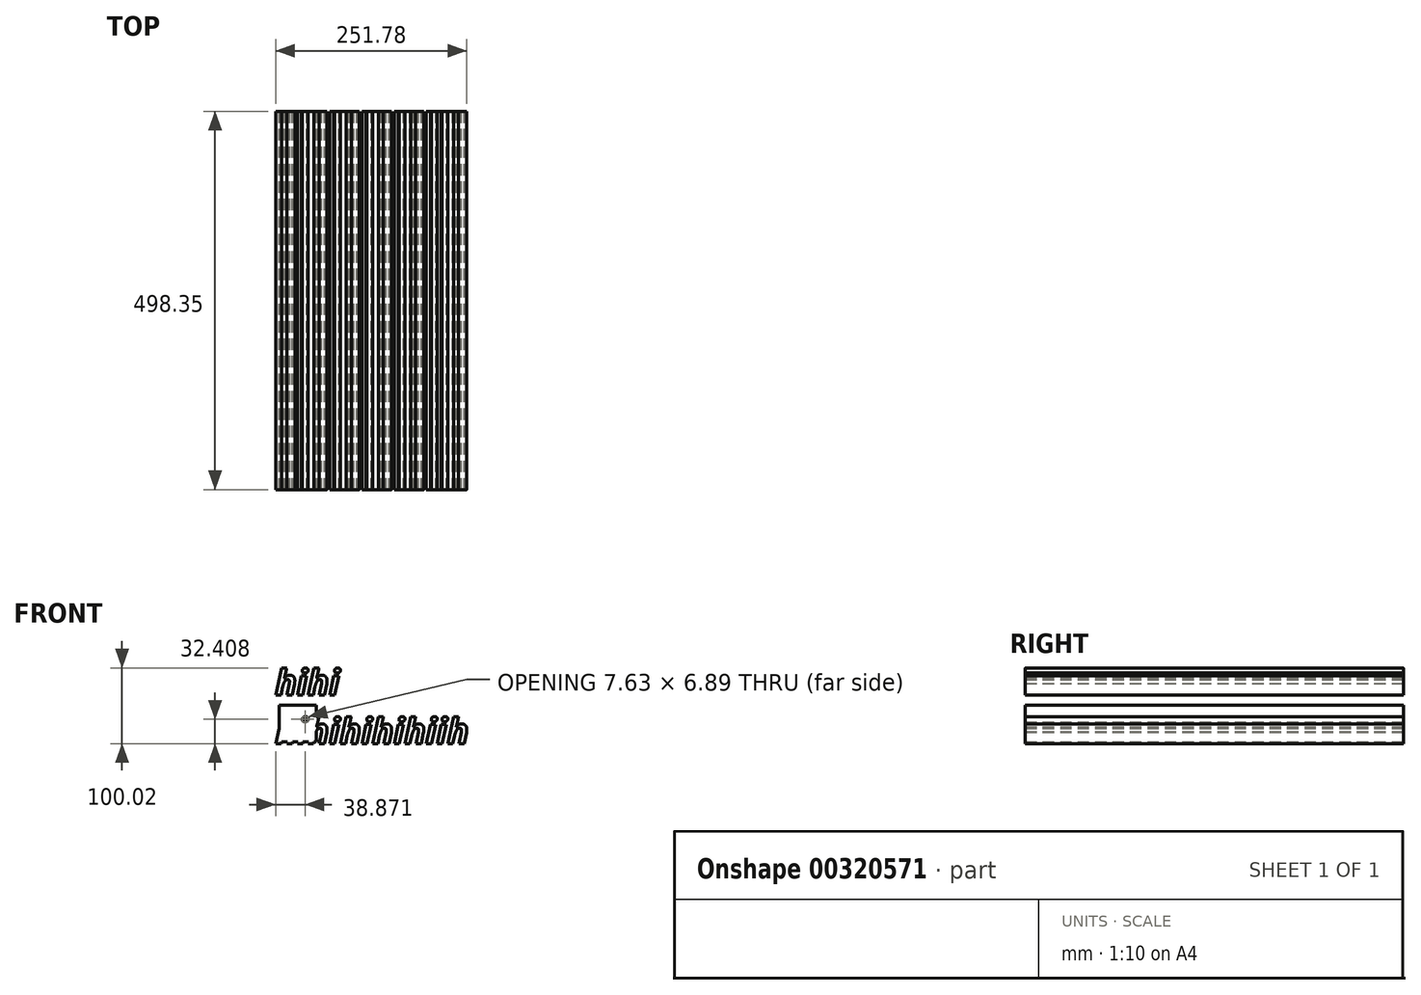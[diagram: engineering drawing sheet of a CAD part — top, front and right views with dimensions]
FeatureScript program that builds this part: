
annotation { "Feature Type Name" : "Feature", "Feature Type Description" : "" }
export const myFeature = defineFeature(function(context is Context, id is Id, definition is map)
    precondition{}
    {
        {
            var Q0;
            Q0=qCreatedBy(makeId("Front.planeOp"),FACE);
            var sketch = newSketch(context, id + "F0", { "sketchPlane" : qUnion([Q0])});
            skLineSegment(sketch, "E0.bottom", {"start": v(24.5, -24.1) * mm, "end": v(-24.5, -24.1) * mm});
            skLineSegment(sketch, "E0.top", {"start": v(24.5, 24.1) * mm, "end": v(-24.5, 24.1) * mm});
            skLineSegment(sketch, "E0.left", {"start": v(24.5, -24.1) * mm, "end": v(24.5, 24.1) * mm});
            skLineSegment(sketch, "E0.right", {"start": v(-24.5, -24.1) * mm, "end": v(-24.5, 24.1) * mm});
            skPoint(sketch, "E0.middle", {"position": v(0, 0) * mm});
            skText(sketch, "E1", { "text": "hihi\nhihihihihiih", "fontName": "OpenSans-BoldItalic.ttf"});
            const initialGuessF0  = {"E1": [-0.02972, 0.03754, 1, 0, 0.03397]};
            skSetInitialGuess(sketch, initialGuessF0);
            skSolve(sketch);
        }
        {
            var Q0;
            {var subQ0=sQuery(id+"F0.wireOp",EDGE,"E0.top");Q0=makeQuery(id+"F0.imprint","IMPRINT",FACE,{"disambiguationData":[TD([[makeQuery(id+"F0.imprint","IMPRINT",EDGE,{"derivedFrom":subQ0}),1.0]])]});}
            var Q1;
            Q1 = qSketchRegion(id + "F0", true);
            var Q2;
            Q2=makeQuery(id+"F0.imprint","IMPRINT",FACE,{"disambiguationData":[TD([[makeQuery(id+"F0.imprint","IMPRINT",EDGE,{"derivedFrom":sQuery(id+"F0.wireOp",EDGE,"E1.sketch_text.stroke-146")}),-1.0]])]});
            extrude(context, id + "F1", {"entities" : qUnion([Q0, Q1, Q2]), "depth" : 498.35 * mm});
        }
    });
